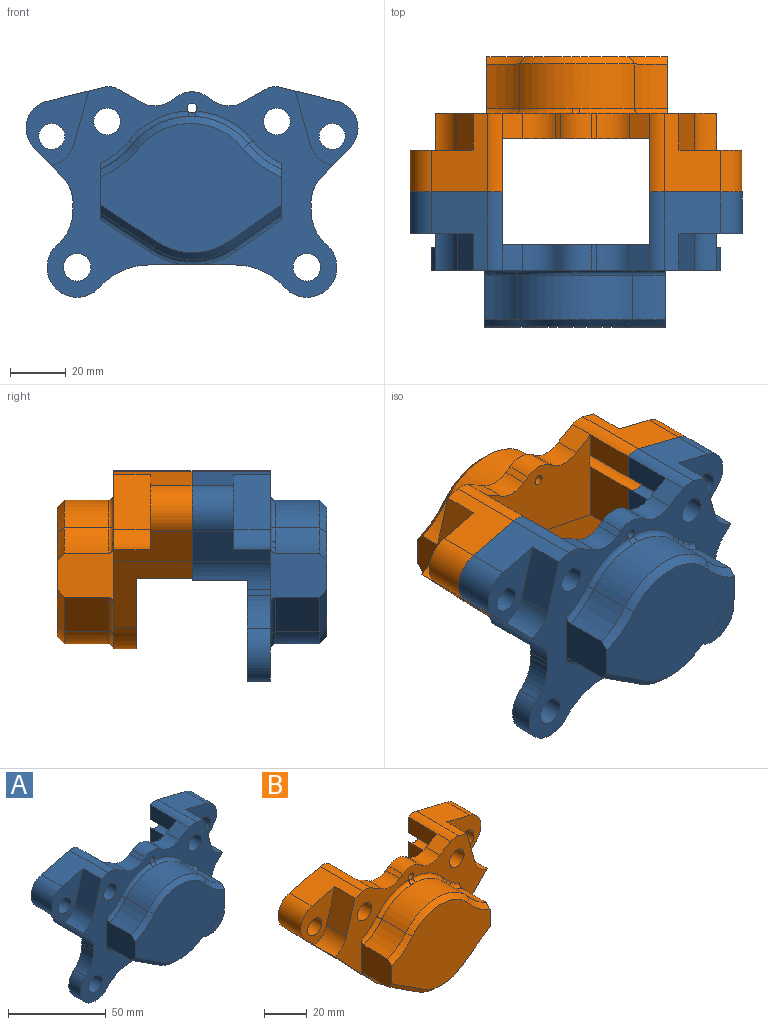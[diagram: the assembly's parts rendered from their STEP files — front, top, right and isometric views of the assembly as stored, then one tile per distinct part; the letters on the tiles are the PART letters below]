
ASSEMBLY  parts=2 mates=1
PART A: 75 faces, bbox 119.9x49.1x76.2 mm
  f0: cylinder r=13.08mm len=28.19mm, axis (0,1,0), area 245.7mm2, adj f1,f3,f15,f19,f26,f70
  f1: plane 104.14x44.92mm, normal (0,1,0), area 2944mm2, adj f0,f14,f15,f16,f25,f65,f66,f67
  f2: plane 39.36x33.19mm, normal (0,1,0), area 828.5mm2, adj f11,f14,f21,f22,f23,f24,f25,f28
  f3: plane 39.36x33.19mm, normal (0,1,0), area 828.5mm2, adj f0,f12,f15,f17,f18,f20,f26,f27
  f4: plane 9.14x7.28mm, normal (-0.49,0,0.87), area 76.4mm2, adj f5,f19,f20,f61
  f5: cylinder r=10.16mm len=11.71mm, axis (0,1,0), area 114.1mm2, adj f4,f6,f19,f61
  f6: plane 9.14x2.07mm, normal (0.58,0,0.82), area 23.2mm2, adj f5,f7,f19,f61
  f7: cylinder r=9.38mm len=10.81mm, axis (0,1,0), area 105.4mm2, adj f6,f8,f19,f61
  f8: plane 9.14x2.07mm, normal (-0.58,0,0.82), area 23.2mm2, adj f7,f9,f19,f61
  f9: cylinder r=10.16mm len=11.71mm, axis (0,1,0), area 114.1mm2, adj f8,f10,f19,f61
  f10: plane 9.14x7.28mm, normal (0.49,0,0.87), area 76.4mm2, adj f9,f19,f21,f61
  f11: cylinder r=4.81mm len=28.19mm, axis (0,1,0), area 749.7mm2, adj f2,f19,f60,f61,f63
  f12: cylinder r=4.81mm len=28.19mm, axis (0,1,0), area 749.7mm2, adj f3,f19,f61,f62,f64
  f13: cylinder r=1.8mm len=9.14mm, axis (0,1,0), area 103.7mm2, adj f19,f46,f61
  f14: plane 42.95x19.81mm, normal (0.2,0,-0.98), area 353.6mm2, adj f1,f2,f15,f25,f61,f63
  f15: plane 42.95x19.81mm, normal (-0.2,0,-0.98), area 353.6mm2, adj f0,f1,f3,f14,f61,f64
  f16: plane 30.48x8.39mm, normal (0,0,-1), area 255.4mm2, adj f1,f19,f51,f73,f74
  f17: cylinder r=9.95mm len=16.57mm, axis (0,1,0), area 312.7mm2, adj f3,f26,f27,f54
  f18: cylinder r=4.69mm len=14.99mm, axis (0,1,0), area 441.3mm2, adj f3,f54
  f19: plane 104.14x75.69mm, normal (0,-1,0), area 2779.7mm2, adj f0,f4,f5,f6,f7,f8,f9,f10
  f20: cylinder r=7.19mm len=28.19mm, axis (0,1,0), area 153.1mm2, adj f3,f4,f19,f27,f62
  f21: cylinder r=7.19mm len=28.19mm, axis (0,1,0), area 153.1mm2, adj f2,f10,f19,f22,f60
  f22: plane 28.19x20.38mm, normal (-0.24,0,0.97), area 386.5mm2, adj f2,f19,f21,f23,f57,f59
  f23: cylinder r=9.95mm len=16.57mm, axis (0,1,0), area 312.7mm2, adj f2,f22,f24,f57
  f24: plane 28.19x10.8mm, normal (-0.72,0,-0.7), area 303.3mm2, adj f2,f19,f23,f25,f57,f58
  f25: cylinder r=13.08mm len=28.19mm, axis (0,1,0), area 245.7mm2, adj f1,f2,f14,f19,f24,f68
  f26: plane 28.19x10.8mm, normal (0.72,0,-0.7), area 303.3mm2, adj f0,f3,f17,f19,f54,f55
  f27: plane 28.19x20.38mm, normal (0.24,0,0.97), area 386.5mm2, adj f3,f17,f19,f20,f54,f56
  f28: cylinder r=4.69mm len=14.99mm, axis (0,1,0), area 441.3mm2, adj f2,f57
  f29: cylinder r=31.65mm len=15.88mm, axis (0,1,0), area 239.5mm2, adj f30,f36,f41,f48
  f30: plane 20.84x20.69mm, normal (-1,0,0), area 315.3mm2, adj f19,f29,f31,f37,f40,f41,f48,f53
  f31: plane 19.05x15.88mm, normal (-0.55,0,-0.84), area 361.2mm2, adj f30,f32,f40,f53
  f32: cylinder r=25.4mm len=28.65mm, axis (0,1,0), area 483.3mm2, adj f31,f33,f39,f50,f51,f52
  f33: plane 17.32x15.88mm, normal (0.57,0,-0.82), area 335.6mm2, adj f32,f34,f38,f49
  f34: plane 20.88x20.78mm, normal (1,0,0), area 315.3mm2, adj f19,f33,f35,f37,f38,f43,f44,f49
  f35: cylinder r=31.65mm len=15.88mm, axis (0,1,0), area 239.5mm2, adj f34,f36,f43,f44
  f36: cylinder r=26.49mm len=41.37mm, axis (0,1,0), area 753.6mm2, adj f29,f35,f42,f45,f46,f47
  f37: plane 65.02x46.5mm, normal (0,-1,0), area 2056.4mm2, adj f30,f34,f38,f39,f40,f41,f42,f43
  f38: plane 18.78x15.22mm, normal (0.41,-0.71,-0.58), area 79.1mm2, adj f33,f34,f37,f39
  f39: cone r=22.86mm half-angle=45deg, axis (0,1,0), area 103.9mm2, adj f32,f37,f38,f40
  f40: plane 20.45x15.48mm, normal (-0.39,-0.71,-0.59), area 84.7mm2, adj f30,f31,f37,f39
  f41: cone r=34.19mm half-angle=45deg, axis (0,-1,0), area 58.3mm2, adj f29,f30,f37,f42
  f42: cone r=23.95mm half-angle=45deg, axis (0,1,0), area 162.4mm2, adj f36,f37,f41,f43
  f43: cone r=34.19mm half-angle=45deg, axis (0,-1,0), area 58.3mm2, adj f34,f35,f37,f42
  f44: torus R=29.74mm, axis (0,1,0), area 42.8mm2, adj f19,f34,f35,f45
  f45: torus R=28.39mm, axis (0,1,0), area 67.7mm2, adj f19,f36,f44,f46
  f46: bspline ~2.87x1.94mm, area 6.7mm2, adj f13,f36,f45,f47
  f47: torus R=28.39mm, axis (0,1,0), area 69.9mm2, adj f19,f36,f46,f48
  f48: torus R=29.74mm, axis (0,1,0), area 42.8mm2, adj f19,f29,f30,f47
  f49: cylinder r=1.91mm len=18.41mm, axis (-0.82,0,-0.57), area 61.3mm2, adj f19,f33,f34,f50
  f50: torus R=27.3mm, axis (0,1,0), area 41.5mm2, adj f19,f32,f49,f51
  f51: bspline ~5.65x1.97mm, area 12.1mm2, adj f16,f32,f50,f52
  f52: torus R=27.3mm, axis (0,1,0), area 39.7mm2, adj f19,f32,f51,f53
  f53: cylinder r=1.91mm len=20.09mm, axis (-0.84,0,0.55), area 66.2mm2, adj f19,f30,f31,f52
  f54: plane 26.84x22.65mm, normal (0,-1,0), area 305.1mm2, adj f17,f18,f26,f27,f55,f56
  f55: cylinder r=10.42mm len=13.21mm, axis (0,-1,0), area 150mm2, adj f19,f26,f54,f56
  f56: plane 19.5x13.21mm, normal (0.96,0,0.28), area 268mm2, adj f19,f27,f54,f55
  f57: plane 26.84x22.65mm, normal (0,-1,0), area 305.1mm2, adj f22,f23,f24,f28,f58,f59
  f58: cylinder r=10.42mm len=13.21mm, axis (0,-1,0), area 150mm2, adj f19,f24,f57,f59
  f59: plane 19.5x13.21mm, normal (-0.96,0,0.28), area 268mm2, adj f19,f22,f57,f58
  f60: plane 19.05x9mm, normal (1,0,0), area 171.5mm2, adj f2,f11,f21,f61
  f61: plane 52.94x35.14mm, normal (0,1,0), area 1519.4mm2, adj f4,f5,f6,f7,f8,f9,f10,f11
  f62: plane 19.05x9mm, normal (-1,0,0), area 171.5mm2, adj f3,f12,f20,f61
  f63: plane 21.03x19.05mm, normal (1,0,0), area 400.7mm2, adj f2,f11,f14,f61
  f64: plane 21.03x19.05mm, normal (-1,0,0), area 400.7mm2, adj f3,f12,f15,f61
  f65: cylinder r=4.95mm len=9.91mm, axis (0,-1,0), area 260.9mm2, adj f1,f19
  f66: cylinder r=4.95mm len=9.91mm, axis (0,-1,0), area 260.9mm2, adj f1,f19
  f67: cylinder r=10.79mm len=19.01mm, axis (0,-1,0), area 296.5mm2, adj f1,f19,f71,f74
  f68: plane 8.38x2.02mm, normal (-1,0,0), area 16.9mm2, adj f1,f19,f25,f71
  f69: cylinder r=10.79mm len=19.01mm, axis (0,-1,0), area 296.5mm2, adj f1,f19,f72,f73
  f70: plane 8.38x2.02mm, normal (1,0,0), area 16.9mm2, adj f0,f1,f19,f72
  f71: cylinder r=15.64mm len=11.9mm, axis (0,-1,0), area 113.4mm2, adj f1,f19,f67,f68
  f72: cylinder r=15.64mm len=11.9mm, axis (0,-1,0), area 113.4mm2, adj f1,f19,f69,f70
  f73: cylinder r=24.13mm len=17.99mm, axis (0,-1,0), area 170.2mm2, adj f1,f16,f19,f69
  f74: cylinder r=24.13mm len=17.99mm, axis (0,-1,0), area 170.2mm2, adj f1,f16,f19,f67
PART B: 71 faces, bbox 119.9x49.1x66.9 mm
  f0: plane 38.86x33.19mm, normal (0,1,0), area 822mm2, adj f9,f12,f21,f22,f23,f24,f25,f29
  f1: plane 38.86x33.19mm, normal (0,1,0), area 822mm2, adj f10,f13,f15,f16,f20,f26,f27,f28
  f2: plane 9.14x7.28mm, normal (-0.49,0,0.87), area 76.4mm2, adj f3,f17,f20,f65
  f3: cylinder r=10.16mm len=11.71mm, axis (0,1,0), area 114.1mm2, adj f2,f4,f17,f65
  f4: plane 9.14x2.07mm, normal (0.58,0,0.82), area 23.2mm2, adj f3,f5,f17,f65
  f5: cylinder r=9.38mm len=10.81mm, axis (0,1,0), area 105.4mm2, adj f4,f6,f17,f65
  f6: plane 9.14x2.07mm, normal (-0.58,0,0.82), area 23.2mm2, adj f5,f7,f17,f65
  f7: cylinder r=10.16mm len=11.71mm, axis (0,1,0), area 114.1mm2, adj f6,f8,f17,f65
  f8: plane 9.14x7.28mm, normal (0.49,0,0.87), area 76.4mm2, adj f7,f17,f21,f65
  f9: cylinder r=4.81mm len=28.19mm, axis (0,1,0), area 749.7mm2, adj f0,f17,f64,f65,f67
  f10: cylinder r=4.81mm len=28.19mm, axis (0,1,0), area 749.7mm2, adj f1,f17,f65,f66,f68
  f11: cylinder r=1.8mm len=9.14mm, axis (0,1,0), area 103.7mm2, adj f17,f47,f65
  f12: plane 40.45x19.81mm, normal (0.2,0,-0.98), area 303.1mm2, adj f0,f13,f25,f63,f65,f67
  f13: plane 40.45x19.81mm, normal (-0.2,0,-0.98), area 303.1mm2, adj f1,f12,f26,f63,f65,f68
  f14: plane 11.1x8.39mm, normal (0,0,-1), area 92.9mm2, adj f18,f19,f53,f63,f69,f70
  f15: cylinder r=9.95mm len=16.57mm, axis (0,1,0), area 312.7mm2, adj f1,f27,f28,f57
  f16: cylinder r=4.69mm len=14.99mm, axis (0,1,0), area 441.3mm2, adj f1,f57
  f17: plane 101.07x47.6mm, normal (0,-1,0), area 1450.8mm2, adj f2,f3,f4,f5,f6,f7,f8,f9
  f18: plane 28.38x14.55mm, normal (0,-1,0), area 51.4mm2, adj f14,f25,f54,f55,f70
  f19: plane 29.07x15.74mm, normal (0,-1,0), area 50.3mm2, adj f14,f26,f51,f52,f69
  f20: cylinder r=7.19mm len=28.19mm, axis (0,1,0), area 153.1mm2, adj f1,f2,f17,f28,f66
  f21: cylinder r=7.19mm len=28.19mm, axis (0,1,0), area 153.1mm2, adj f0,f8,f17,f22,f64
  f22: plane 28.19x20.38mm, normal (-0.24,0,0.97), area 386.5mm2, adj f0,f17,f21,f23,f60,f62
  f23: cylinder r=9.95mm len=16.57mm, axis (0,1,0), area 312.7mm2, adj f0,f22,f24,f60
  f24: plane 28.19x10.8mm, normal (-0.72,0,-0.7), area 303.3mm2, adj f0,f17,f23,f25,f60,f61
  f25: plane 28.23x23.6mm, normal (-0.72,0,-0.69), area 444.4mm2, adj f0,f12,f17,f18,f24,f56,f63,f70
  f26: plane 28.2x23.57mm, normal (0.72,0,-0.69), area 444.4mm2, adj f1,f13,f17,f19,f27,f50,f63,f69
  f27: plane 28.19x10.8mm, normal (0.72,0,-0.7), area 303.3mm2, adj f1,f15,f17,f26,f57,f58
  f28: plane 28.19x20.38mm, normal (0.24,0,0.97), area 386.5mm2, adj f1,f15,f17,f20,f57,f59
  f29: cylinder r=4.69mm len=14.99mm, axis (0,1,0), area 441.3mm2, adj f0,f60
  f30: cylinder r=31.65mm len=15.88mm, axis (0,1,0), area 239.5mm2, adj f31,f37,f42,f49
  f31: plane 20.7x19.52mm, normal (-1,0,0), area 314.9mm2, adj f17,f30,f32,f38,f41,f42,f49,f56
  f32: plane 19.05x16.16mm, normal (-0.55,0,-0.84), area 361.6mm2, adj f31,f33,f41,f55,f56
  f33: cylinder r=25.4mm len=28.65mm, axis (0,1,0), area 483.3mm2, adj f32,f34,f40,f52,f53,f54
  f34: plane 17.32x15.92mm, normal (0.57,0,-0.82), area 335.7mm2, adj f33,f35,f39,f50,f51
  f35: plane 20.9x20.57mm, normal (1,0,0), area 315.2mm2, adj f17,f34,f36,f38,f39,f44,f45,f50
  f36: cylinder r=31.65mm len=15.88mm, axis (0,1,0), area 239.5mm2, adj f35,f37,f44,f45
  f37: cylinder r=26.49mm len=41.37mm, axis (0,1,0), area 753.6mm2, adj f30,f36,f43,f46,f47,f48
  f38: plane 65.02x46.5mm, normal (0,-1,0), area 2056.4mm2, adj f31,f35,f39,f40,f41,f42,f43,f44
  f39: plane 18.78x15.22mm, normal (0.41,-0.71,-0.58), area 79.1mm2, adj f34,f35,f38,f40
  f40: cone r=22.86mm half-angle=45deg, axis (0,1,0), area 103.9mm2, adj f33,f38,f39,f41
  f41: plane 20.45x15.48mm, normal (-0.39,-0.71,-0.59), area 84.7mm2, adj f31,f32,f38,f40
  f42: cone r=34.19mm half-angle=45deg, axis (0,-1,0), area 58.3mm2, adj f30,f31,f38,f43
  f43: cone r=23.95mm half-angle=45deg, axis (0,1,0), area 162.4mm2, adj f37,f38,f42,f44
  f44: cone r=34.19mm half-angle=45deg, axis (0,-1,0), area 58.3mm2, adj f35,f36,f38,f43
  f45: torus R=29.74mm, axis (0,1,0), area 42.8mm2, adj f17,f35,f36,f46
  f46: torus R=28.39mm, axis (0,1,0), area 67.7mm2, adj f17,f37,f45,f47
  f47: bspline ~2.87x1.94mm, area 6.7mm2, adj f11,f37,f46,f48
  f48: torus R=28.39mm, axis (0,1,0), area 69.9mm2, adj f17,f37,f47,f49
  f49: torus R=29.74mm, axis (0,1,0), area 42.8mm2, adj f17,f30,f31,f48
  f50: bspline ~3.44x3.31mm, area 4.3mm2, adj f26,f34,f35,f51
  f51: cylinder r=1.91mm len=16.66mm, axis (-0.82,0,-0.57), area 56.9mm2, adj f19,f34,f50,f52
  f52: torus R=27.3mm, axis (0,1,0), area 41.5mm2, adj f19,f33,f51,f53
  f53: bspline ~5.65x1.97mm, area 12.1mm2, adj f14,f33,f52,f54
  f54: torus R=27.3mm, axis (0,1,0), area 39.7mm2, adj f18,f33,f53,f55
  f55: cylinder r=1.91mm len=16.44mm, axis (-0.84,0,0.55), area 55mm2, adj f18,f32,f54,f56
  f56: bspline ~3.98x3.98mm, area 10.1mm2, adj f25,f31,f32,f55
  f57: plane 26.84x22.65mm, normal (0,-1,0), area 305.1mm2, adj f15,f16,f27,f28,f58,f59
  f58: cylinder r=10.42mm len=13.21mm, axis (0,-1,0), area 150mm2, adj f17,f27,f57,f59
  f59: plane 19.5x13.21mm, normal (0.96,0,0.28), area 268mm2, adj f17,f28,f57,f58
  f60: plane 26.84x22.65mm, normal (0,-1,0), area 305.1mm2, adj f22,f23,f24,f29,f61,f62
  f61: cylinder r=10.42mm len=13.21mm, axis (0,-1,0), area 150mm2, adj f17,f24,f60,f62
  f62: plane 19.5x13.21mm, normal (-0.96,0,0.28), area 268mm2, adj f17,f22,f60,f61
  f63: plane 80.9x33.26mm, normal (0,1,0), area 1728.2mm2, adj f12,f13,f14,f25,f26,f69,f70
  f64: plane 19.05x9mm, normal (1,0,0), area 171.5mm2, adj f0,f9,f21,f65
  f65: plane 52.94x35.14mm, normal (0,1,0), area 1519.4mm2, adj f2,f3,f4,f5,f6,f7,f8,f9
  f66: plane 19.05x9mm, normal (-1,0,0), area 171.5mm2, adj f1,f10,f20,f65
  f67: plane 21.03x19.05mm, normal (1,0,0), area 400.7mm2, adj f0,f9,f12,f65
  f68: plane 21.03x19.05mm, normal (-1,0,0), area 400.7mm2, adj f1,f10,f13,f65
  f69: cylinder r=25.4mm len=18.37mm, axis (0,1,0), area 172.1mm2, adj f14,f19,f26,f63
  f70: cylinder r=25.4mm len=18.37mm, axis (0,1,0), area 172.1mm2, adj f14,f18,f25,f63
PLACE A t=(-43.98,-61.74,-38.26)mm
PLACE B rot(axis=(0,0,1),180deg) t=(-67.04,-61.74,-38.26)mm
MATE fastened B.f16 <-> A.f28  axis (0,-1,0) through (-105.86,-61.74,38.13)mm
